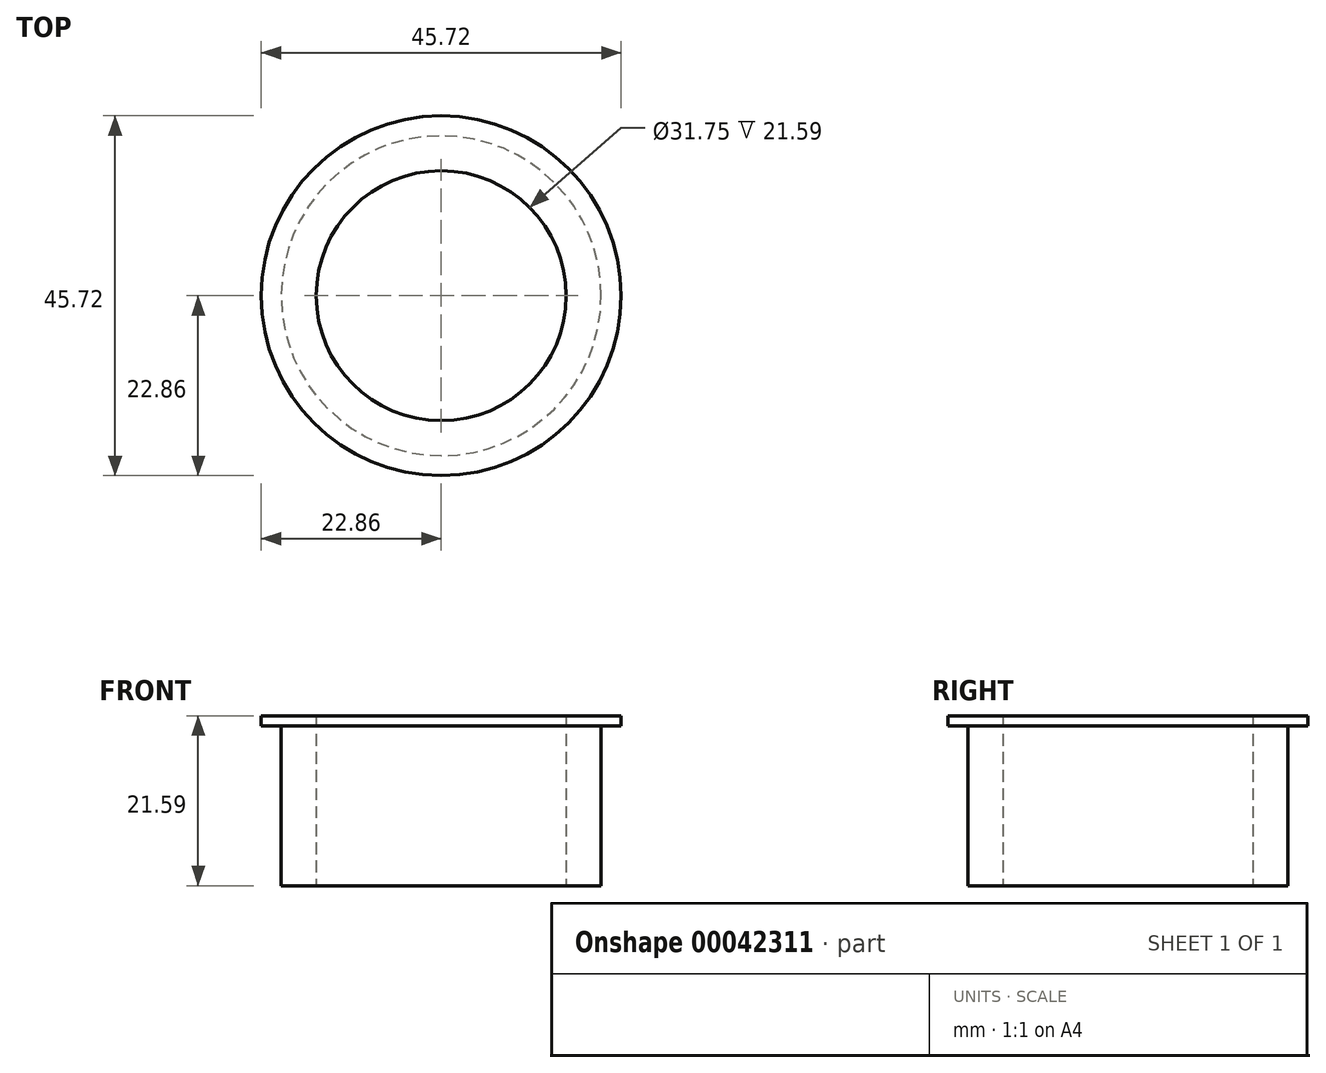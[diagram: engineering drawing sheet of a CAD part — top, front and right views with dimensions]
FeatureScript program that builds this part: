
annotation { "Feature Type Name" : "Feature", "Feature Type Description" : "" }
export const myFeature = defineFeature(function(context is Context, id is Id, definition is map)
    precondition{}
    {
        {
            var Q0;
            Q0=qCreatedBy(makeId("Top.planeOp"),FACE);
            var sketch = newSketch(context, id + "F0", { "sketchPlane" : qUnion([Q0])});
            skCircle(sketch, "E0", {"center": v(0, 0) * mm, "radius": 20.32 * mm});
            skCircle(sketch, "E1", {"center": v(0, 0) * mm, "radius": 15.88 * mm});
            skSolve(sketch);
        }
        {
            var Q0;
            Q0=makeQuery(id+"F0.imprint","IMPRINT",FACE,{"disambiguationData":[TD([[makeQuery(id+"F0.imprint","IMPRINT",EDGE,{"derivedFrom":sQuery(id+"F0.wireOp",EDGE,"E0")}),1.0]])]});
            extrude(context, id + "F1", {"entities" : qUnion([Q0]), "depth" : 20.32 * mm});
        }
        {
            var Q0;
            Q0=makeQuery(id+"F1.opExtrude","CAP_FACE",FACE,{"disambiguationData":[OSD([sQuery(id+"F0.wireOp",EDGE,"E0"),sQuery(id+"F0.wireOp",EDGE,"E1")])],"isStart":false});
            var sketch = newSketch(context, id + "F2", { "sketchPlane" : qUnion([Q0])});
            skCircle(sketch, "E2", {"center": v(0, 0) * mm, "radius": 22.86 * mm});
            skSolve(sketch);
        }
        {
            var Q0;
            Q0=makeQuery(id+"F2.imprint","IMPRINT",FACE,{"disambiguationData":[TD([[makeQuery(id+"F2.imprint","IMPRINT",EDGE,{"derivedFrom":sQuery(id+"F2.wireOp",EDGE,"E2")}),1.0]])]});
            var Q1;
            Q1=makeQuery(id+"F2.imprint","IMPRINT",FACE,{"disambiguationData":[TD([[makeQuery(id+"F2.imprint","IMPRINT",EDGE,{"derivedFrom":makeQuery(id+"F1.opExtrude","CAP_EDGE",EDGE,{"disambiguationData":[OSD([sQuery(id+"F0.wireOp",EDGE,"E0")])],"isStart":false})}),1.0]])]});
            extrude(context, id + "F3", {"entities" : qUnion([Q0, Q1]), "operationType" : NewBodyOperationType.ADD, "depth" : 1.27 * mm});
        }
    });
